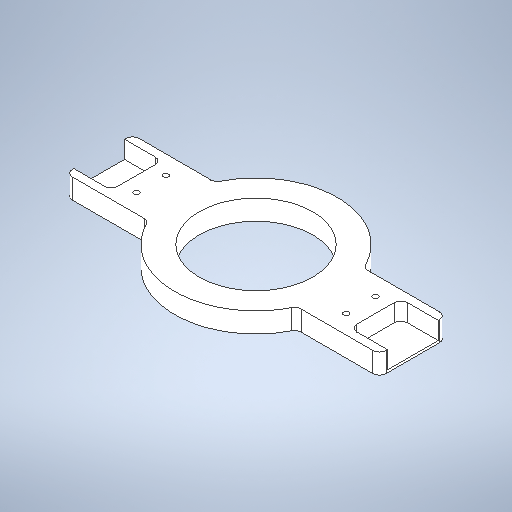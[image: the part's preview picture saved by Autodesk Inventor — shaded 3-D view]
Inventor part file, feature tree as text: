
AUTODESK INVENTOR PART (.ipt)
format: ipt  version: 2025 (Build 290162000, 162)  size: 294,912 bytes
history: native  units: mm
features: sketch x3, extrude x2, mirror x2, hole x1, fillet x1, plane x1
ambient origin geometry x8: Origin, YZ Plane, XZ Plane, XY Plane, X Axis, Y Axis, Z Axis, Center Point
bodies: Solid1 (feature_tree)
feature tree (10):
  extrude  "Extrusion1"  Depth=15.0mm TaperAngle=0.0deg
  extrude  "Extrusion2"  Depth=38.0mm
  mirror  "Mirror1"
  hole  "Hole1"  [1 undecoded]
  mirror  "Mirror2"
  fillet  "Fillet1"  Radius=39.0mm
  sketch  "Sketch1"  dims[d0=85.0mm d1=61.0mm d2=235.0mm d3=50.0mm d4=15.0mm d5=0.0mm]
  sketch  "Sketch2"  dims[d6=5.0mm d7=38.0mm]
  plane  "Work Plane1"
  sketch  "Sketch3"  dims[d8=28.0mm d9=13.1mm d10=0.0mm d11=4.0mm d12=6.0mm d13=8.0mm d14=6.0mm d15=90.0deg d16=3.0mm d17=0.0mm d19=39.0mm d22=11.0mm d23=5.0mm]
note: 1 required parameter value undecoded (feature->parameter linkage not recoverable at this tier; creation-order binding heuristic only, values carry confidence <= 0.55)
